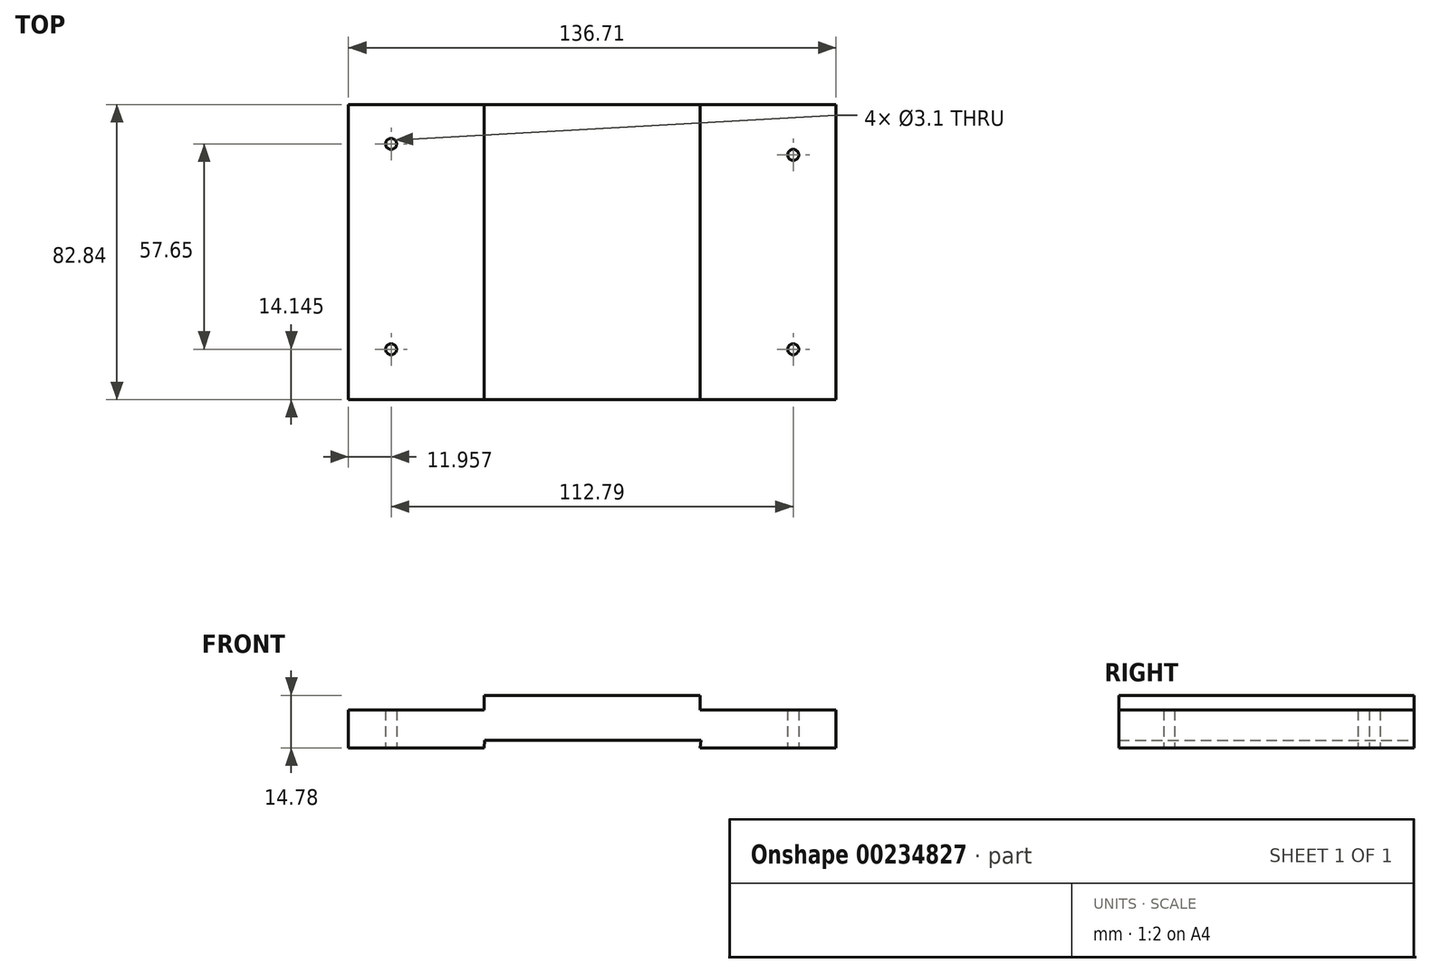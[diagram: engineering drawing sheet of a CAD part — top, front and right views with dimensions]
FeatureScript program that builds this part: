
annotation { "Feature Type Name" : "Feature", "Feature Type Description" : "" }
export const myFeature = defineFeature(function(context is Context, id is Id, definition is map)
    precondition{}
    {
        {
            var Q0;
            Q0=qCreatedBy(makeId("Front.planeOp"),FACE);
            var sketch = newSketch(context, id + "F0", { "sketchPlane" : qUnion([Q0])});
            skLineSegment(sketch, "E0", {"start": v(-60.82, 18.29) * mm, "end": v(-22.75, 18.29) * mm});
            skLineSegment(sketch, "E1", {"start": v(-22.75, 18.29) * mm, "end": v(-22.75, 22.34) * mm});
            skLineSegment(sketch, "E2", {"start": v(-22.75, 22.34) * mm, "end": v(37.82, 22.34) * mm});
            skLineSegment(sketch, "E3", {"start": v(37.82, 22.34) * mm, "end": v(37.82, 18.29) * mm});
            skLineSegment(sketch, "E4", {"start": v(37.82, 18.29) * mm, "end": v(75.89, 18.29) * mm});
            skLineSegment(sketch, "E5", {"start": v(75.89, 18.29) * mm, "end": v(75.89, 7.58) * mm});
            skLineSegment(sketch, "E6", {"start": v(-60.82, 18.29) * mm, "end": v(-60.82, 7.56) * mm});
            skLineSegment(sketch, "E7", {"start": v(-60.82, 7.56) * mm, "end": v(-22.75, 7.56) * mm});
            skLineSegment(sketch, "E8", {"start": v(75.89, 7.58) * mm, "end": v(37.82, 7.58) * mm});
            skLineSegment(sketch, "E9", {"start": v(-22.63, 9.7) * mm, "end": v(38.02, 9.7) * mm});
            skLineSegment(sketch, "E10", {"start": v(-22.63, 9.7) * mm, "end": v(-22.75, 7.56) * mm});
            skLineSegment(sketch, "E11", {"start": v(38.02, 9.7) * mm, "end": v(37.82, 7.58) * mm});
            skSolve(sketch);
        }
        {
            var Q0;
            Q0 = qSketchRegion(id + "F0", true);
            extrude(context, id + "F1", {"entities" : qUnion([Q0]), "endBound" : BoundingType.SYMMETRIC, "depth" : 82.85 * mm});
        }
        {
            var Q0;
            Q0=qCreatedBy(makeId("Top.planeOp"),FACE);
            var sketch = newSketch(context, id + "F2", { "sketchPlane" : qUnion([Q0])});
            skCircle(sketch, "E12", {"center": v(-48.86, 30.37) * mm, "radius": 1.55 * mm});
            skCircle(sketch, "E13", {"center": v(63.93, 27.28) * mm, "radius": 1.55 * mm});
            skCircle(sketch, "E14", {"center": v(63.93, -27.27) * mm, "radius": 1.55 * mm});
            skCircle(sketch, "E15", {"center": v(-48.86, -27.27) * mm, "radius": 1.55 * mm});
            skSolve(sketch);
        }
        {
            var Q0;
            Q0 = qSketchRegion(id + "F2", true);
            extrude(context, id + "F3", {"entities" : qUnion([Q0]), "operationType" : NewBodyOperationType.REMOVE, "endBound" : BoundingType.THROUGH_ALL, "depth" : 25 * mm});
        }
    });
